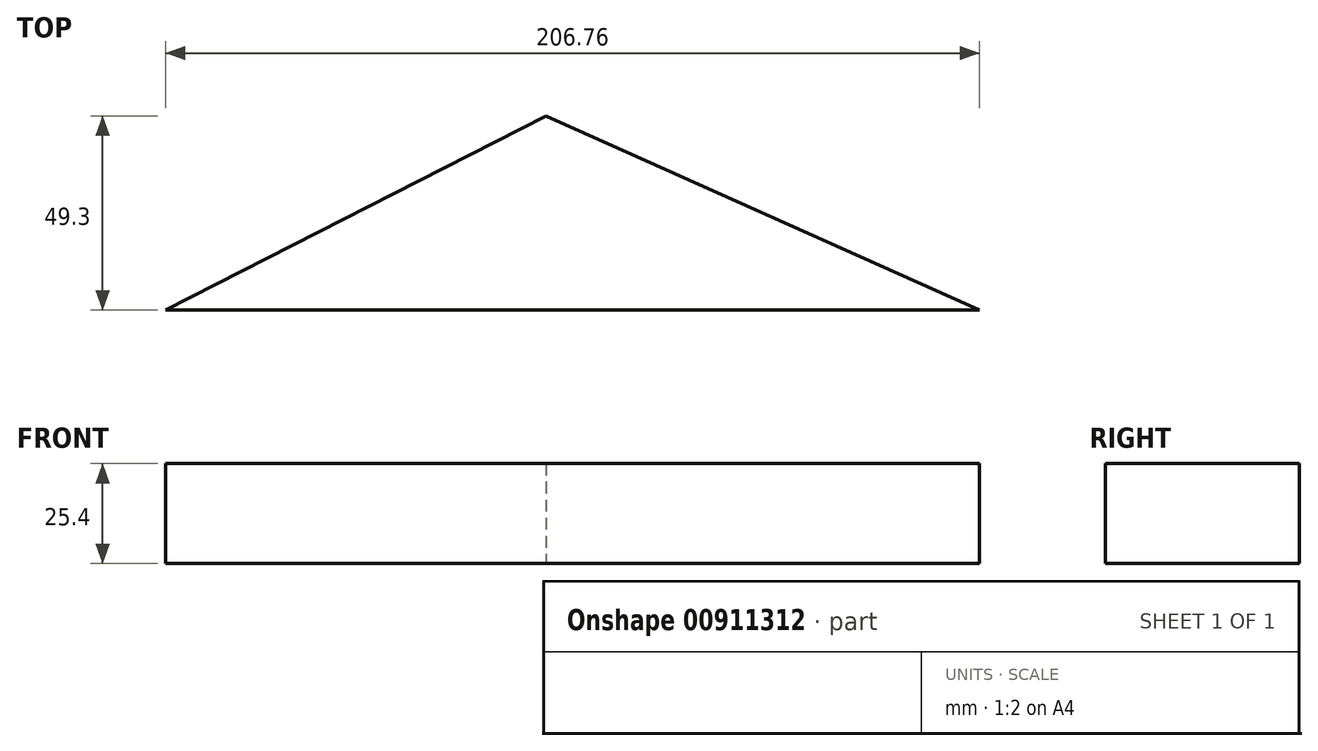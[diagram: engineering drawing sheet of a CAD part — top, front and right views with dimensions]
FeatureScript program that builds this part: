
annotation { "Feature Type Name" : "Feature", "Feature Type Description" : "" }
export const myFeature = defineFeature(function(context is Context, id is Id, definition is map)
    precondition{}
    {
        {
            var Q0;
            Q0=qCreatedBy(makeId("Top.planeOp"),FACE);
            var sketch = newSketch(context, id + "F0", { "sketchPlane" : qUnion([Q0])});
            skLineSegment(sketch, "E0.bottom", {"start": v(-96.64, 59.78) * mm, "end": v(110.12, 59.78) * mm});
            skLineSegment(sketch, "E0.top", {"start": v(-96.64, -49.3) * mm, "end": v(110.12, -49.3) * mm});
            skLineSegment(sketch, "E0.left", {"start": v(-96.64, 59.78) * mm, "end": v(-96.64, -49.3) * mm});
            skLineSegment(sketch, "E0.right", {"start": v(110.12, 59.78) * mm, "end": v(110.12, -49.3) * mm});
            skLineSegment(sketch, "E1", {"start": v(-96.64, 59.78) * mm, "end": v(0, 0) * mm});
            skLineSegment(sketch, "E2", {"start": v(110.12, 59.78) * mm, "end": v(0, 0) * mm});
            skLineSegment(sketch, "E3", {"start": v(0, 0) * mm, "end": v(110.12, -49.3) * mm});
            skLineSegment(sketch, "E4", {"start": v(0, 0) * mm, "end": v(-96.64, -49.3) * mm});
            skSolve(sketch);
        }
        {
            var Q0;
            Q0=makeQuery(id+"F0.imprint","IMPRINT",FACE,{"disambiguationData":[TD([[makeQuery(id+"F0.imprint","IMPRINT",EDGE,{"derivedFrom":sQuery(id+"F0.wireOp",EDGE,"E0.top")}),1.0]])]});
            extrude(context, id + "F1", {"entities" : qUnion([Q0]), "depth" : 25.4 * mm, "offsetDistance" : 25.4 * mm});
        }
    });
